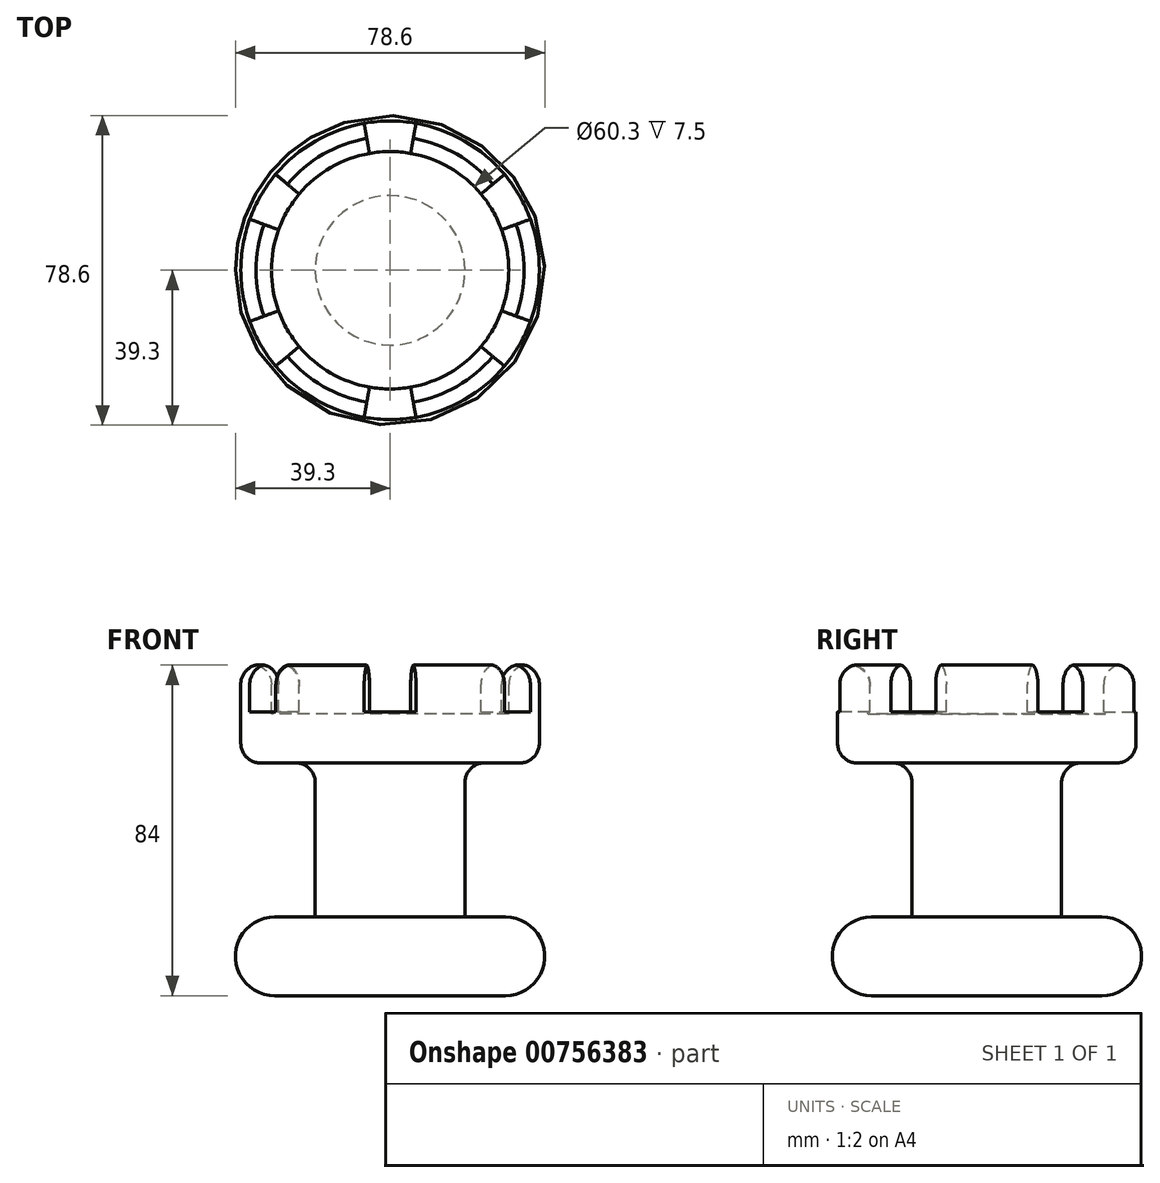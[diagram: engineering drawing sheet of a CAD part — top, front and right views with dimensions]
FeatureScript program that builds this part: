
annotation { "Feature Type Name" : "Feature", "Feature Type Description" : "" }
export const myFeature = defineFeature(function(context is Context, id is Id, definition is map)
    precondition{}
    {
        {
            var Q0;
            Q0=qCreatedBy(makeId("Front.planeOp"),FACE);
            var sketch = newSketch(context, id + "F0", { "sketchPlane" : qUnion([Q0])});
            skLineSegment(sketch, "E0.bottom", {"start": v(0, 0) * mm, "end": v(39.3, 0) * mm});
            skLineSegment(sketch, "E0.top", {"start": v(19, 20) * mm, "end": v(39.3, 20) * mm});
            skLineSegment(sketch, "E0.left", {"start": v(0, 0) * mm, "end": v(0, 20) * mm});
            skLineSegment(sketch, "E0.right", {"start": v(39.3, 0) * mm, "end": v(39.3, 20) * mm});
            skLineSegment(sketch, "E1.bottom", {"start": v(0, 0) * mm, "end": v(19, 0) * mm});
            skLineSegment(sketch, "E1.left", {"start": v(0, 0) * mm, "end": v(0, 59.13) * mm});
            skLineSegment(sketch, "E1.right", {"start": v(19, 20) * mm, "end": v(19, 59.13) * mm});
            skLineSegment(sketch, "E2.bottom", {"start": v(19, 59.13) * mm, "end": v(37.92, 59.13) * mm});
            skLineSegment(sketch, "E2.top", {"start": v(0, 84.13) * mm, "end": v(37.92, 84.13) * mm});
            skLineSegment(sketch, "E2.left", {"start": v(0, 59.13) * mm, "end": v(0, 84.13) * mm});
            skLineSegment(sketch, "E2.right", {"start": v(37.92, 59.13) * mm, "end": v(37.92, 84.13) * mm});
            skSolve(sketch);
        }
        {
            var Q0;
            Q0=makeQuery(id+"F0.imprint","IMPRINT",FACE,{"disambiguationData":[TD([[makeQuery(id+"F0.imprint","IMPRINT",EDGE,{"derivedFrom":sQuery(id+"F0.wireOp",EDGE,"E0.bottom")}),1.0]])]});
            var Q1;
            Q1=sQuery(id+"F0.wireOp",EDGE,"E1.left");
            revolve(context, id + "F1", {"surfaceOperationType" : NewSurfaceOperationType.NEW, "entities" : qUnion([Q0]), "axis" : qUnion([Q1]), "revolveType" : RevolveType.FULL});
        }
        {
            var Q0;
            Q0=makeQuery(id+"F1.opRevolve","SWEPT_FACE",FACE,{"disambiguationData":[OSD([sQuery(id+"F0.wireOp",EDGE,"E2.top")])]});
            var sketch = newSketch(context, id + "F2", { "sketchPlane" : qUnion([Q0])});
            skCircle(sketch, "E3", {"center": v(0, 0) * mm, "radius": 30.15 * mm});
            skSolve(sketch);
        }
        {
            var Q0;
            Q0=makeQuery(id+"F2.imprint","IMPRINT",FACE,{"disambiguationData":[TD([[makeQuery(id+"F2.imprint","IMPRINT",EDGE,{"derivedFrom":sQuery(id+"F2.wireOp",EDGE,"E3")}),1.0]])]});
            extrude(context, id + "F3", {"entities" : qUnion([Q0]), "operationType" : NewBodyOperationType.REMOVE, "endBound" : BoundingType.SYMMETRIC, "oppositeDirection" : true, "depth" : 25 * mm, "offsetDistance" : 25 * mm});
        }
        {
            var Q0;
            Q0=makeQuery(id+"F1.opRevolve","SWEPT_FACE",FACE,{"disambiguationData":[OSD([sQuery(id+"F0.wireOp",EDGE,"E2.top")])]});
            var sketch = newSketch(context, id + "F4", { "sketchPlane" : qUnion([Q0])});
            skLineSegment(sketch, "E4", {"start": v(4.28, 24.28) * mm, "end": v(8.04, 45.62) * mm});
            skLineSegment(sketch, "E5", {"start": v(-4.28, 24.28) * mm, "end": v(-8.04, 45.62) * mm});
            skArc(sketch, "E6", {"start": v(4.28, 24.28) * mm, "mid": v(0, 24.65) * mm, "end": v(-4.28, 24.28) * mm});
            skArc(sketch, "E7", {"start": v(8.04, 45.62) * mm, "mid": v(0, 46.33) * mm, "end": v(-8.04, 45.62) * mm});
            skArc(sketch, "E8.1.0", {"start": v(-18.89, 15.85) * mm, "mid": v(-21.35, 12.33) * mm, "end": v(-23.17, 8.43) * mm});
            skLineSegment(sketch, "E8.1.1", {"start": v(-23.17, 8.43) * mm, "end": v(-43.53, 15.84) * mm});
            skArc(sketch, "E8.1.2", {"start": v(-35.49, 29.78) * mm, "mid": v(-40.12, 23.16) * mm, "end": v(-43.53, 15.84) * mm});
            skLineSegment(sketch, "E8.1.3", {"start": v(-18.89, 15.85) * mm, "end": v(-35.49, 29.78) * mm});
            skArc(sketch, "E8.2.0", {"start": v(-23.17, -8.43) * mm, "mid": v(-21.35, -12.33) * mm, "end": v(-18.89, -15.85) * mm});
            skLineSegment(sketch, "E8.2.1", {"start": v(-18.89, -15.85) * mm, "end": v(-35.49, -29.78) * mm});
            skArc(sketch, "E8.2.2", {"start": v(-43.53, -15.84) * mm, "mid": v(-40.12, -23.16) * mm, "end": v(-35.49, -29.78) * mm});
            skLineSegment(sketch, "E8.2.3", {"start": v(-23.17, -8.43) * mm, "end": v(-43.53, -15.84) * mm});
            skArc(sketch, "E8.3.0", {"start": v(-4.28, -24.28) * mm, "mid": v(0, -24.65) * mm, "end": v(4.28, -24.28) * mm});
            skLineSegment(sketch, "E8.3.1", {"start": v(4.28, -24.28) * mm, "end": v(8.04, -45.62) * mm});
            skArc(sketch, "E8.3.2", {"start": v(-8.04, -45.62) * mm, "mid": v(0, -46.33) * mm, "end": v(8.04, -45.62) * mm});
            skLineSegment(sketch, "E8.3.3", {"start": v(-4.28, -24.28) * mm, "end": v(-8.04, -45.62) * mm});
            skArc(sketch, "E8.4.0", {"start": v(18.89, -15.85) * mm, "mid": v(21.35, -12.33) * mm, "end": v(23.17, -8.43) * mm});
            skLineSegment(sketch, "E8.4.1", {"start": v(23.17, -8.43) * mm, "end": v(43.53, -15.84) * mm});
            skArc(sketch, "E8.4.2", {"start": v(35.49, -29.78) * mm, "mid": v(40.12, -23.16) * mm, "end": v(43.53, -15.84) * mm});
            skLineSegment(sketch, "E8.4.3", {"start": v(18.89, -15.85) * mm, "end": v(35.49, -29.78) * mm});
            skArc(sketch, "E8.5.0", {"start": v(23.17, 8.43) * mm, "mid": v(21.35, 12.33) * mm, "end": v(18.89, 15.85) * mm});
            skLineSegment(sketch, "E8.5.1", {"start": v(18.89, 15.85) * mm, "end": v(35.49, 29.78) * mm});
            skArc(sketch, "E8.5.2", {"start": v(43.53, 15.84) * mm, "mid": v(40.12, 23.16) * mm, "end": v(35.49, 29.78) * mm});
            skLineSegment(sketch, "E8.5.3", {"start": v(23.17, 8.43) * mm, "end": v(43.53, 15.84) * mm});
            skSolve(sketch);
        }
        {
            var Q0;
            Q0 = qSketchRegion(id + "F4", true);
            extrude(context, id + "F5", {"entities" : qUnion([Q0]), "operationType" : NewBodyOperationType.REMOVE, "oppositeDirection" : true, "depth" : 12 * mm, "offsetDistance" : 25 * mm});
        }
        {
            var Q0;
            Q0=makeQuery(id+"F1.opRevolve","SWEPT_EDGE",EDGE,{"disambiguationData":[OSD([sQuery(id+"F0.wireOp",EDGE,"E0.top"),sQuery(id+"F0.wireOp",EDGE,"E0.right")])]});
            var Q1;
            Q1=makeQuery(id+"F1.opRevolve","SWEPT_EDGE",EDGE,{"disambiguationData":[OSD([sQuery(id+"F0.wireOp",EDGE,"E0.bottom"),sQuery(id+"F0.wireOp",EDGE,"E0.right")])]});
            fillet(context, id + "F6", {"entities" : qUnion([Q0, Q1]), "radius" : 10 * mm, "tangentPropagation" : true, "allowEdgeOverflow" : false});
        }
        {
            var Q0;
            {var subQ0=sQuery(id+"F0.wireOp",EDGE,"E2.top");var subQ1=sQuery(id+"F0.wireOp",EDGE,"E2.right");Q0=makeQuery(id+"F5.boolean.opBoolean","SPLIT",EDGE,{"disambiguationData":[TD([makeQuery(id+"F5.opExtrude","SWEPT_FACE",FACE,{"disambiguationData":[OSD([sQuery(id+"F4.wireOp",EDGE,"E8.3.1")])]})])],"derivedFrom":makeQuery(id+"F1.opRevolve","SWEPT_EDGE",EDGE,{"disambiguationData":[OSD([subQ0,subQ1])]})});}
            var Q1;
            {var subQ0=makeQuery(id+"F1.opRevolve","SWEPT_FACE",FACE,{"disambiguationData":[OSD([sQuery(id+"F0.wireOp",EDGE,"E2.top")])]});var subQ1=makeQuery(id+"F3.opExtrude","SWEPT_FACE",FACE,{"disambiguationData":[OSD([sQuery(id+"F2.wireOp",EDGE,"E3")])]});Q1=makeQuery(id+"F5.boolean.opBoolean","SPLIT",EDGE,{"disambiguationData":[TD([makeQuery(id+"F5.opExtrude","SWEPT_FACE",FACE,{"disambiguationData":[OSD([sQuery(id+"F4.wireOp",EDGE,"E8.3.1")])]})])],"derivedFrom":makeQuery(id+"F3.boolean.opBoolean","INTERSECT",EDGE,{"derivedFrom":[subQ0,subQ1]})});}
            fillet(context, id + "F7", {"entities" : qUnion([Q0, Q1]), "radius" : 5 * mm, "tangentPropagation" : true, "allowEdgeOverflow" : false});
        }
        {
            var Q0;
            {var subQ0=sQuery(id+"F0.wireOp",EDGE,"E2.top");var subQ1=sQuery(id+"F0.wireOp",EDGE,"E2.right");Q0=makeQuery(id+"F5.boolean.opBoolean","SPLIT",EDGE,{"disambiguationData":[TD([makeQuery(id+"F5.opExtrude","SWEPT_FACE",FACE,{"disambiguationData":[OSD([sQuery(id+"F4.wireOp",EDGE,"E8.2.1")])]})])],"derivedFrom":makeQuery(id+"F1.opRevolve","SWEPT_EDGE",EDGE,{"disambiguationData":[OSD([subQ0,subQ1])]})});}
            var Q1;
            {var subQ0=makeQuery(id+"F1.opRevolve","SWEPT_FACE",FACE,{"disambiguationData":[OSD([sQuery(id+"F0.wireOp",EDGE,"E2.top")])]});var subQ1=makeQuery(id+"F3.opExtrude","SWEPT_FACE",FACE,{"disambiguationData":[OSD([sQuery(id+"F2.wireOp",EDGE,"E3")])]});Q1=makeQuery(id+"F5.boolean.opBoolean","SPLIT",EDGE,{"disambiguationData":[TD([makeQuery(id+"F5.opExtrude","SWEPT_FACE",FACE,{"disambiguationData":[OSD([sQuery(id+"F4.wireOp",EDGE,"E8.2.1")])]})])],"derivedFrom":makeQuery(id+"F3.boolean.opBoolean","INTERSECT",EDGE,{"derivedFrom":[subQ0,subQ1]})});}
            fillet(context, id + "F8", {"entities" : qUnion([Q0, Q1]), "radius" : 5.55 * mm, "tangentPropagation" : true, "allowEdgeOverflow" : false});
        }
        {
            var Q0;
            {var subQ0=makeQuery(id+"F1.opRevolve","SWEPT_FACE",FACE,{"disambiguationData":[OSD([sQuery(id+"F0.wireOp",EDGE,"E2.top")])]});var subQ1=makeQuery(id+"F3.opExtrude","SWEPT_FACE",FACE,{"disambiguationData":[OSD([sQuery(id+"F2.wireOp",EDGE,"E3")])]});Q0=makeQuery(id+"F5.boolean.opBoolean","SPLIT",EDGE,{"disambiguationData":[TD([makeQuery(id+"F5.opExtrude","SWEPT_FACE",FACE,{"disambiguationData":[OSD([sQuery(id+"F4.wireOp",EDGE,"E8.1.1")])]})])],"derivedFrom":makeQuery(id+"F3.boolean.opBoolean","INTERSECT",EDGE,{"derivedFrom":[subQ0,subQ1]})});}
            var Q1;
            {var subQ0=sQuery(id+"F0.wireOp",EDGE,"E2.top");var subQ1=sQuery(id+"F0.wireOp",EDGE,"E2.right");Q1=makeQuery(id+"F5.boolean.opBoolean","SPLIT",EDGE,{"disambiguationData":[TD([makeQuery(id+"F5.opExtrude","SWEPT_FACE",FACE,{"disambiguationData":[OSD([sQuery(id+"F4.wireOp",EDGE,"E8.1.1")])]})])],"derivedFrom":makeQuery(id+"F1.opRevolve","SWEPT_EDGE",EDGE,{"disambiguationData":[OSD([subQ0,subQ1])]})});}
            fillet(context, id + "F9", {"entities" : qUnion([Q0, Q1]), "radius" : 5 * mm, "tangentPropagation" : true, "allowEdgeOverflow" : false});
        }
        {
            var Q0;
            {var subQ0=makeQuery(id+"F1.opRevolve","SWEPT_FACE",FACE,{"disambiguationData":[OSD([sQuery(id+"F0.wireOp",EDGE,"E2.top")])]});var subQ1=makeQuery(id+"F3.opExtrude","SWEPT_FACE",FACE,{"disambiguationData":[OSD([sQuery(id+"F2.wireOp",EDGE,"E3")])]});Q0=makeQuery(id+"F5.boolean.opBoolean","SPLIT",EDGE,{"disambiguationData":[TD([makeQuery(id+"F5.opExtrude","SWEPT_FACE",FACE,{"disambiguationData":[OSD([sQuery(id+"F4.wireOp",EDGE,"E8.4.1")])]})])],"derivedFrom":makeQuery(id+"F3.boolean.opBoolean","INTERSECT",EDGE,{"derivedFrom":[subQ0,subQ1]})});}
            var Q1;
            {var subQ0=sQuery(id+"F0.wireOp",EDGE,"E2.top");var subQ1=sQuery(id+"F0.wireOp",EDGE,"E2.right");Q1=makeQuery(id+"F5.boolean.opBoolean","SPLIT",EDGE,{"disambiguationData":[TD([makeQuery(id+"F5.opExtrude","SWEPT_FACE",FACE,{"disambiguationData":[OSD([sQuery(id+"F4.wireOp",EDGE,"E8.4.1")])]})])],"derivedFrom":makeQuery(id+"F1.opRevolve","SWEPT_EDGE",EDGE,{"disambiguationData":[OSD([subQ0,subQ1])]})});}
            fillet(context, id + "F10", {"entities" : qUnion([Q0, Q1]), "radius" : 5 * mm, "tangentPropagation" : true, "allowEdgeOverflow" : false});
        }
        {
            var Q0;
            {var subQ0=makeQuery(id+"F1.opRevolve","SWEPT_FACE",FACE,{"disambiguationData":[OSD([sQuery(id+"F0.wireOp",EDGE,"E2.top")])]});var subQ1=makeQuery(id+"F3.opExtrude","SWEPT_FACE",FACE,{"disambiguationData":[OSD([sQuery(id+"F2.wireOp",EDGE,"E3")])]});Q0=makeQuery(id+"F5.boolean.opBoolean","SPLIT",EDGE,{"disambiguationData":[TD([makeQuery(id+"F5.opExtrude","SWEPT_FACE",FACE,{"disambiguationData":[OSD([sQuery(id+"F4.wireOp",EDGE,"E4")])]})])],"derivedFrom":makeQuery(id+"F3.boolean.opBoolean","INTERSECT",EDGE,{"derivedFrom":[subQ0,subQ1]})});}
            var Q1;
            {var subQ0=sQuery(id+"F0.wireOp",EDGE,"E2.top");var subQ1=sQuery(id+"F0.wireOp",EDGE,"E2.right");Q1=makeQuery(id+"F5.boolean.opBoolean","SPLIT",EDGE,{"disambiguationData":[TD([makeQuery(id+"F5.opExtrude","SWEPT_FACE",FACE,{"disambiguationData":[OSD([sQuery(id+"F4.wireOp",EDGE,"E4")])]})])],"derivedFrom":makeQuery(id+"F1.opRevolve","SWEPT_EDGE",EDGE,{"disambiguationData":[OSD([subQ0,subQ1])]})});}
            fillet(context, id + "F11", {"entities" : qUnion([Q0, Q1]), "radius" : 5 * mm, "tangentPropagation" : true, "allowEdgeOverflow" : false});
        }
        {
            var Q0;
            {var subQ0=makeQuery(id+"F1.opRevolve","SWEPT_FACE",FACE,{"disambiguationData":[OSD([sQuery(id+"F0.wireOp",EDGE,"E2.top")])]});var subQ1=makeQuery(id+"F3.opExtrude","SWEPT_FACE",FACE,{"disambiguationData":[OSD([sQuery(id+"F2.wireOp",EDGE,"E3")])]});Q0=makeQuery(id+"F5.boolean.opBoolean","SPLIT",EDGE,{"disambiguationData":[TD([makeQuery(id+"F5.opExtrude","SWEPT_FACE",FACE,{"disambiguationData":[OSD([sQuery(id+"F4.wireOp",EDGE,"E5")])]})])],"derivedFrom":makeQuery(id+"F3.boolean.opBoolean","INTERSECT",EDGE,{"derivedFrom":[subQ0,subQ1]})});}
            var Q1;
            {var subQ0=sQuery(id+"F0.wireOp",EDGE,"E2.top");var subQ1=sQuery(id+"F0.wireOp",EDGE,"E2.right");Q1=makeQuery(id+"F5.boolean.opBoolean","SPLIT",EDGE,{"disambiguationData":[TD([makeQuery(id+"F5.opExtrude","SWEPT_FACE",FACE,{"disambiguationData":[OSD([sQuery(id+"F4.wireOp",EDGE,"E5")])]})])],"derivedFrom":makeQuery(id+"F1.opRevolve","SWEPT_EDGE",EDGE,{"disambiguationData":[OSD([subQ0,subQ1])]})});}
            fillet(context, id + "F12", {"entities" : qUnion([Q0, Q1]), "radius" : 5 * mm, "tangentPropagation" : true, "allowEdgeOverflow" : false});
        }
        {
            var Q0;
            Q0=makeQuery(id+"F1.opRevolve","SWEPT_EDGE",EDGE,{"disambiguationData":[OSD([sQuery(id+"F0.wireOp",EDGE,"E2.bottom"),sQuery(id+"F0.wireOp",EDGE,"E2.right")])]});
            var Q1;
            Q1=makeQuery(id+"F1.opRevolve","SWEPT_EDGE",EDGE,{"disambiguationData":[OSD([sQuery(id+"F0.wireOp",EDGE,"E1.right"),sQuery(id+"F0.wireOp",EDGE,"E2.bottom")])]});
            fillet(context, id + "F13", {"entities" : qUnion([Q0, Q1]), "radius" : 5 * mm, "tangentPropagation" : true, "allowEdgeOverflow" : false});
        }
    });
